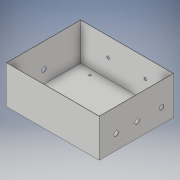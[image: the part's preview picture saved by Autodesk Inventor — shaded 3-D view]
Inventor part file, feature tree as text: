
AUTODESK INVENTOR PART (.ipt)
format: ipt  version: 2018 (Build 220112000, 112)  size: 158,208 bytes
history: native  units: in
note: dims shown in document units (in); Inventor stores cm internally (conversion verified against a paired STEP export)
features: extrude x6, sketch x6
ambient origin geometry x8: Origin, YZ Plane, XZ Plane, XY Plane, X Axis, Y Axis, Z Axis, Center Point
bodies: Solid1 (feature_tree)
feature tree (12):
  extrude  "Extrusion1"  Depth=4.0in
  extrude  "Extrusion2"  Depth=4.96in
  extrude  "Extrusion3"  Depth=2.0in TaperAngle=0.0deg
  extrude  "Extrusion4"  Depth=0.164in
  extrude  "Extrusion5"  Depth=0.25in
  extrude  "Extrusion6"  Depth=0.0115in
  sketch  "Sketch1"  dims[d0=5.0in d1=4.0in]
  sketch  "Sketch2"  dims[d2=0.04in d3=0.0in d4=4.96in]
  sketch  "Sketch3"  dims[d5=3.96in d6=2.0in d7=0.0in]
  sketch  "Sketch4"  dims[d10=0.164in d12=0.164in]
  sketch  "Sketch5"  dims[d13=0.0in d14=0.0in d15=0.25in]
  sketch  "Sketch6"  dims[d16=0.0in d17=0.0in d18=0.0115in d19=0.0in d20=0.625in d21=1.313in d22=180.0deg d23=1.125in d24=0.0in d25=1.125in d26=0.25in d27=0.25in d28=0.25in d29=0.0in d30=0.0in d31=3.937in d32=3.937in d38=0.112in d39=0.112in d40=0.112in d41=0.112in d42=0.0in d43=0.0in]
